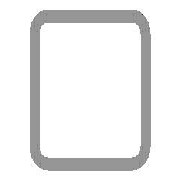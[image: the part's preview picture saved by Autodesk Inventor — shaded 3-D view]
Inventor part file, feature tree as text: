
AUTODESK INVENTOR PART (.ipt)
format: ipt  version: 2025 (Build 290162010, 162A)  size: 134,144 bytes
history: native  units: mm (DEFAULTED — no unit token found)
features: other x4, sketch x1, plane x1
ambient origin geometry x8: Origin, YZ Plane, XZ Plane, XY Plane, X Axis, Y Axis, Z Axis, Center Point
bodies: Solid1 (feature_tree), Body (feature_tree)
feature tree (6):
  parser-record x1  (decoder bookkeeping rows leaked as tree rows — omitted from the tree; the rows remain in map.json)
  other  "Driven Length"
  other  "Start Plane"
  other  "End Plane"
  sketch  "Sketch3"  dims[d3=898.0mm d4=0.0mm d7=4.0mm d9=40.0mm d11=40.0mm d12=2.0mm d13=40.0mm d14=938.0mm d15=20.0mm d16=20.0mm d17=90.0deg d18=898.0mm]
  plane  "Work Plane3"
